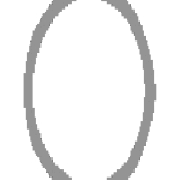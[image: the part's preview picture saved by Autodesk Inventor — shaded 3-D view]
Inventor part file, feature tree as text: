
AUTODESK INVENTOR PART (.ipt)
format: ipt  version: 2021 (Build 250183000, 183)  size: 110,080 bytes
history: native  units: in
note: dims shown in document units (in); Inventor stores cm internally (conversion verified against a paired STEP export)
features: other x4, sketch x3, plane x1
ambient origin geometry x8: Origin, YZ Plane, XZ Plane, XY Plane, X Axis, Y Axis, Z Axis, Center Point
bodies: Solid1 (feature_tree), Body (feature_tree)
feature tree (8):
  other  "Driven Length"
  other  "Frame Generator"
  other  "Start Plane"
  other  "End Plane"
  sketch  "Sketch"  dims[d2=18.4803in d4=-0.0in d5=18.4803in d6=0.12in d7=0.0in d8=90.0deg d9=18.4803in]
  sketch  "Sketch2"  dims[d0=1.0in]
  plane  "Work Plane3"
  sketch  "Sketch3"  dims[d1=0.065in]
